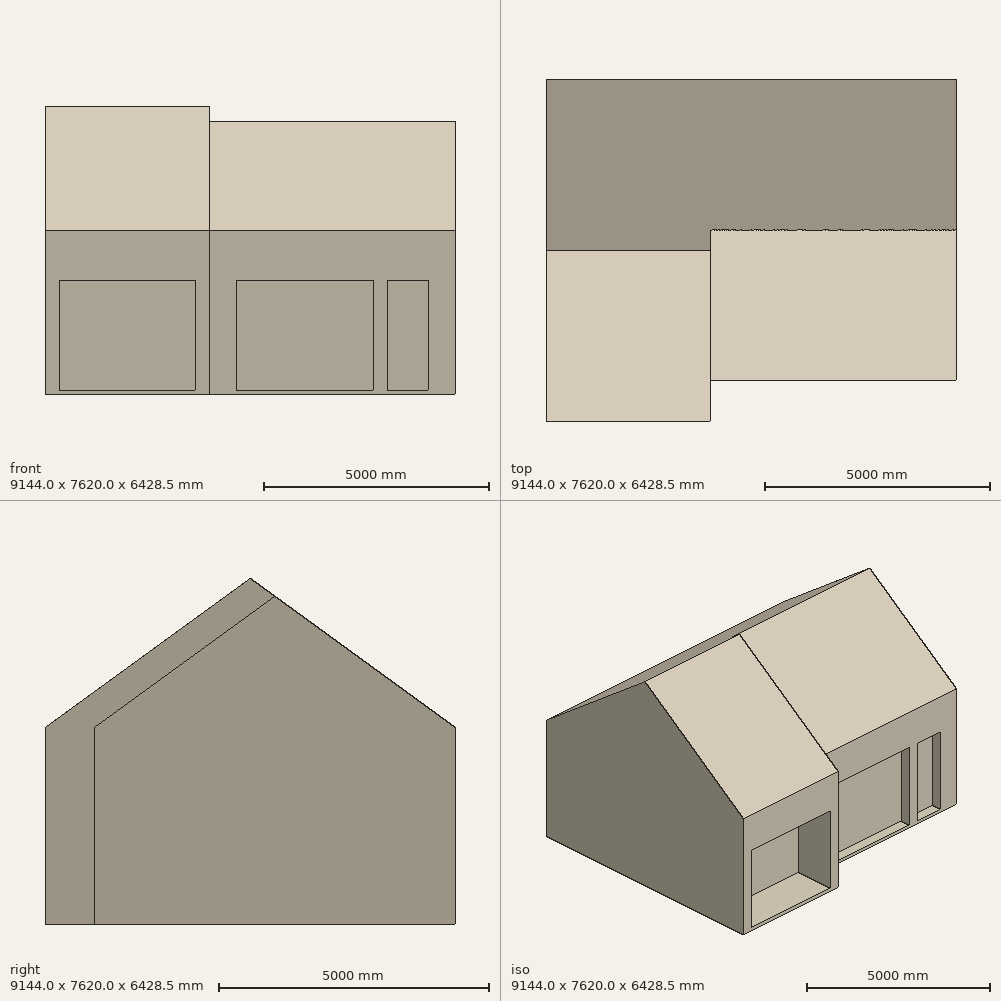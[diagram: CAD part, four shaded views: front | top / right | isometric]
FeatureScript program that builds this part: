
annotation { "Feature Type Name" : "Feature", "Feature Type Description" : "" }
export const myFeature = defineFeature(function(context is Context, id is Id, definition is map)
    precondition{}
    {
        {
            var Q0;
            Q0=qCreatedBy(makeId("Top.planeOp"),FACE);
            var sketch = newSketch(context, id + "F0", { "sketchPlane" : qUnion([Q0])});
            skLineSegment(sketch, "E0", {"start": v(0, 0) * mm, "end": v(9144, 0) * mm});
            skLineSegment(sketch, "E1", {"start": v(9144, 0) * mm, "end": v(9144, -6705.6) * mm});
            skLineSegment(sketch, "E2", {"start": v(9144, -6705.6) * mm, "end": v(3657.6, -6705.6) * mm});
            skLineSegment(sketch, "E3", {"start": v(3657.6, -6705.6) * mm, "end": v(3657.6, -7620) * mm});
            skLineSegment(sketch, "E4", {"start": v(3657.6, -7620) * mm, "end": v(0, -7620) * mm});
            skLineSegment(sketch, "E5", {"start": v(0, -7620) * mm, "end": v(0, 0) * mm});
            skSolve(sketch);
        }
        {
            var Q0;
            Q0=makeQuery(id+"F0.imprint","IMPRINT",FACE,{"disambiguationData":[TD([[makeQuery(id+"F0.imprint","IMPRINT",EDGE,{"derivedFrom":sQuery(id+"F0.wireOp",EDGE,"E0")}),-1.0]])]});
            extrude(context, id + "F1", {"entities" : qUnion([Q0]), "depth" : 3657.6 * mm, "offsetDistance" : 25.4 * mm});
        }
        {
            var Q0;
            Q0=makeQuery(id+"F1.opExtrude","SWEPT_FACE",FACE,{"disambiguationData":[OSD([sQuery(id+"F0.wireOp",EDGE,"E1")])]});
            var sketch = newSketch(context, id + "F2", { "sketchPlane" : qUnion([Q0])});
            skLineSegment(sketch, "E6", {"start": v(-6705.6, 3657.6) * mm, "end": v(-3352.8, 6096) * mm});
            skLineSegment(sketch, "E7", {"start": v(-3352.8, 6096) * mm, "end": v(0, 3657.6) * mm});
            skLineSegment(sketch, "E8", {"start": v(0, 3657.6) * mm, "end": v(-6705.6, 3657.6) * mm});
            skSolve(sketch);
        }
        {
            var Q0;
            Q0=makeQuery(id+"F2.imprint","IMPRINT",FACE,{"disambiguationData":[TD([[makeQuery(id+"F2.imprint","IMPRINT",EDGE,{"derivedFrom":sQuery(id+"F2.wireOp",EDGE,"E6")}),-1.0]])]});
            var Q1;
            Q1=makeQuery(id+"F1.opExtrude","SWEPT_FACE",FACE,{"disambiguationData":[OSD([sQuery(id+"F0.wireOp",EDGE,"E3")])]});
            extrude(context, id + "F3", {"entities" : qUnion([Q0]), "operationType" : NewBodyOperationType.ADD, "endBound" : BoundingType.UP_TO_SURFACE, "oppositeDirection" : true, "depth" : 25.4 * mm, "endBoundEntityFace" : qUnion([Q1]), "offsetDistance" : 25.4 * mm});
        }
        {
            var Q0;
            Q0=makeQuery(id+"F1.opExtrude","SWEPT_FACE",FACE,{"disambiguationData":[OSD([sQuery(id+"F0.wireOp",EDGE,"E5")])]});
            var sketch = newSketch(context, id + "F4", { "sketchPlane" : qUnion([Q0])});
            skLineSegment(sketch, "E9", {"start": v(0, 3657.6) * mm, "end": v(3810, 6428.5) * mm});
            skLineSegment(sketch, "E10", {"start": v(3810, 6428.5) * mm, "end": v(7620, 3657.6) * mm});
            skLineSegment(sketch, "E11", {"start": v(7620, 3657.6) * mm, "end": v(0, 3657.6) * mm});
            skSolve(sketch);
        }
        {
            var Q0;
            Q0 = qSketchRegion(id + "F4", true);
            var Q1;
            Q1=makeQuery(id+"F3.opExtrude","CAP_FACE",FACE,{"disambiguationData":[OSD([sQuery(id+"F2.wireOp",EDGE,"E6"),sQuery(id+"F2.wireOp",EDGE,"E7"),sQuery(id+"F2.wireOp",EDGE,"E8")])],"isStart":false});
            extrude(context, id + "F5", {"entities" : qUnion([Q0]), "operationType" : NewBodyOperationType.ADD, "endBound" : BoundingType.UP_TO_SURFACE, "oppositeDirection" : true, "depth" : 25.4 * mm, "endBoundEntityFace" : qUnion([Q1]), "offsetDistance" : 25.4 * mm});
        }
        {
            var Q0;
            Q0=makeQuery(id+"F1.opExtrude","SWEPT_FACE",FACE,{"disambiguationData":[OSD([sQuery(id+"F0.wireOp",EDGE,"E4")])]});
            var sketch = newSketch(context, id + "F6", { "sketchPlane" : qUnion([Q0])});
            skLineSegment(sketch, "E12.bottom", {"start": v(304.8, 101.6) * mm, "end": v(3352.8, 101.6) * mm});
            skLineSegment(sketch, "E12.top", {"start": v(304.8, 2540) * mm, "end": v(3352.8, 2540) * mm});
            skLineSegment(sketch, "E12.left", {"start": v(304.8, 101.6) * mm, "end": v(304.8, 2540) * mm});
            skLineSegment(sketch, "E12.right", {"start": v(3352.8, 101.6) * mm, "end": v(3352.8, 2540) * mm});
            skLineSegment(sketch, "E13.bottom", {"start": v(4267.2, 101.6) * mm, "end": v(7315.2, 101.6) * mm});
            skLineSegment(sketch, "E13.top", {"start": v(4267.2, 2540) * mm, "end": v(7315.2, 2540) * mm});
            skLineSegment(sketch, "E13.left", {"start": v(4267.2, 101.6) * mm, "end": v(4267.2, 2540) * mm});
            skLineSegment(sketch, "E13.right", {"start": v(7315.2, 101.6) * mm, "end": v(7315.2, 2540) * mm});
            skLineSegment(sketch, "E14.bottom", {"start": v(7620, 2540) * mm, "end": v(8534.4, 2540) * mm});
            skLineSegment(sketch, "E14.top", {"start": v(7620, 101.6) * mm, "end": v(8534.4, 101.6) * mm});
            skLineSegment(sketch, "E14.left", {"start": v(7620, 2540) * mm, "end": v(7620, 101.6) * mm});
            skLineSegment(sketch, "E14.right", {"start": v(8534.4, 2540) * mm, "end": v(8534.4, 101.6) * mm});
            skSolve(sketch);
        }
        {
            var Q0;
            Q0 = qSketchRegion(id + "F6", true);
            extrude(context, id + "F7", {"entities" : qUnion([Q0]), "operationType" : NewBodyOperationType.REMOVE, "oppositeDirection" : true, "depth" : 1219.2 * mm, "offsetDistance" : 25.4 * mm});
        }
    });
